AUTODESK INVENTOR PART (.ipt)
format: ipt  version: 2021 (Build 250183000, 183)  size: 131,584 bytes
history: native  units: mm
features: extrude x2, sketch x1
ambient origin geometry x8: Origin, YZ Plane, XZ Plane, XY Plane, X Axis, Y Axis, Z Axis, Center Point
bodies: Solid1 (feature_tree)
feature tree (3):
  sketch  "Sketch1"  dims[d10=550.0mm d11=360.0mm d12=550.0mm d13=360.0mm d14=360.0mm d15=360.0mm d16=400.0mm d22=3.0mm d23=0.0mm d26=20.0mm d27=20.0mm d28=3.1mm d29=0.0mm]
  extrude  "Extrusion1"  Depth=3.1mm
  extrude  "Extrusion2"  Depth=3.1mm
